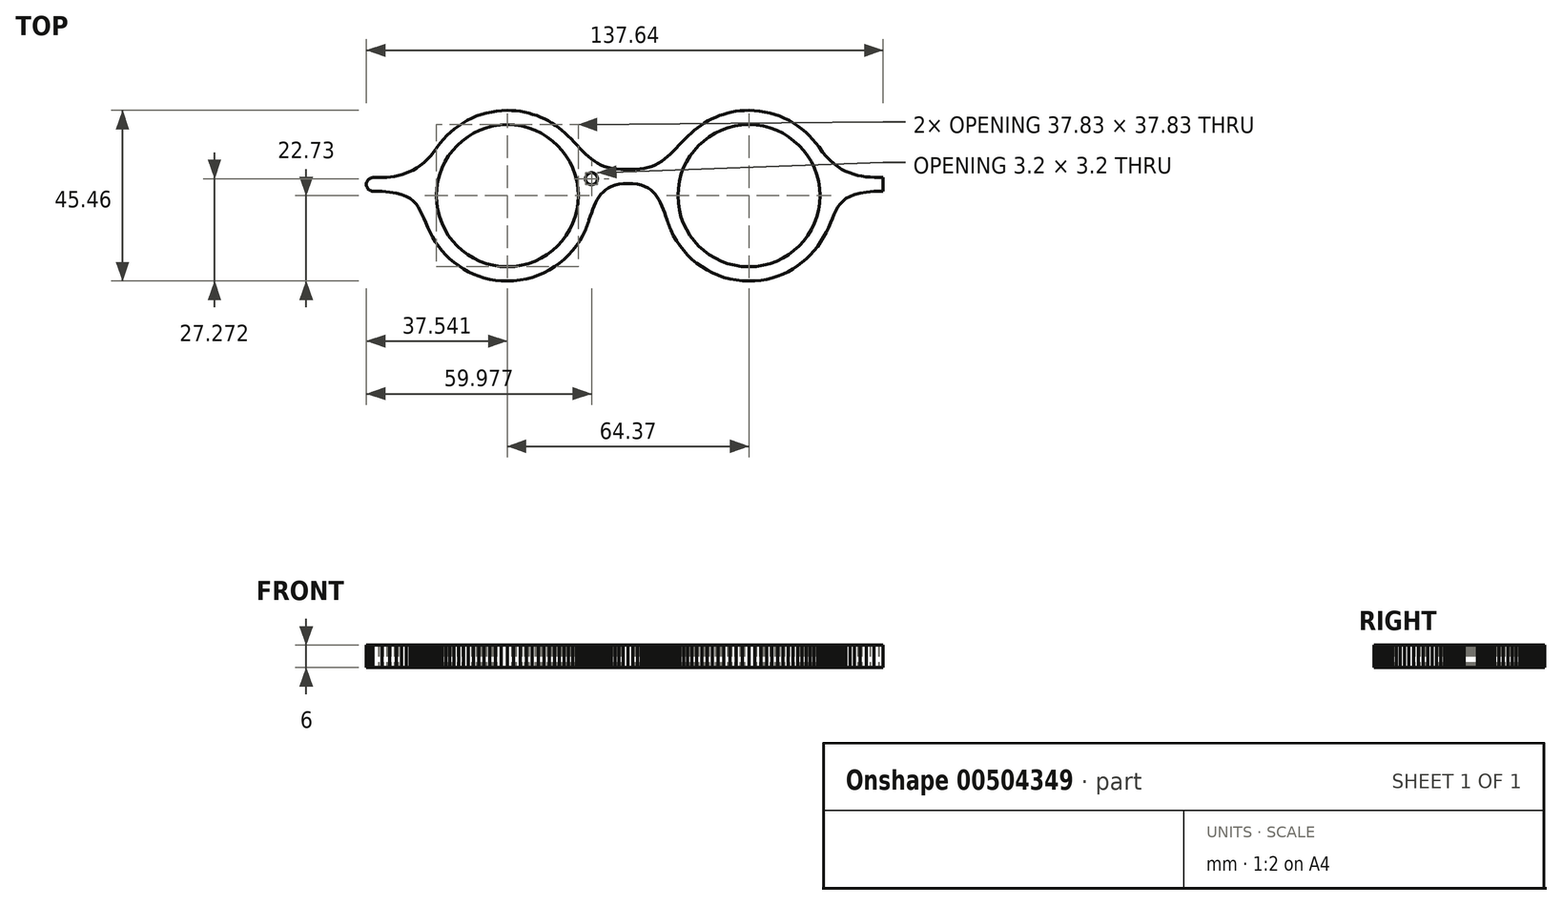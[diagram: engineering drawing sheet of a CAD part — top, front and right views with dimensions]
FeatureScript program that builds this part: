
annotation { "Feature Type Name" : "Feature", "Feature Type Description" : "" }
export const myFeature = defineFeature(function(context is Context, id is Id, definition is map)
    precondition{}
    {
        {
            var Q0;
            Q0=qCreatedBy(makeId("Top.planeOp"),FACE);
            var sketch = newSketch(context, id + "F0", { "sketchPlane" : qUnion([Q0])});
            skLineSegment(sketch, "E0", {"start": v(67.67, 4.85) * mm, "end": v(66.53, 4.88) * mm});
            skLineSegment(sketch, "E1", {"start": v(66.53, 4.88) * mm, "end": v(65.4, 4.94) * mm});
            skLineSegment(sketch, "E2", {"start": v(65.4, 4.94) * mm, "end": v(64.27, 5.05) * mm});
            skLineSegment(sketch, "E3", {"start": v(64.27, 5.05) * mm, "end": v(63.16, 5.2) * mm});
            skLineSegment(sketch, "E4", {"start": v(63.16, 5.2) * mm, "end": v(62.05, 5.43) * mm});
            skLineSegment(sketch, "E5", {"start": v(62.05, 5.43) * mm, "end": v(60.96, 5.72) * mm});
            skLineSegment(sketch, "E6", {"start": v(60.96, 5.72) * mm, "end": v(59.88, 6.09) * mm});
            skLineSegment(sketch, "E7", {"start": v(59.88, 6.09) * mm, "end": v(58.8, 6.54) * mm});
            skLineSegment(sketch, "E8", {"start": v(58.8, 6.54) * mm, "end": v(57.75, 7.1) * mm});
            skLineSegment(sketch, "E9", {"start": v(57.75, 7.1) * mm, "end": v(56.71, 7.75) * mm});
            skLineSegment(sketch, "E10", {"start": v(56.71, 7.75) * mm, "end": v(55.69, 8.53) * mm});
            skLineSegment(sketch, "E11", {"start": v(55.69, 8.53) * mm, "end": v(54.68, 9.43) * mm});
            skLineSegment(sketch, "E12", {"start": v(54.68, 9.43) * mm, "end": v(53.68, 10.46) * mm});
            skLineSegment(sketch, "E13", {"start": v(53.68, 10.46) * mm, "end": v(52.7, 11.64) * mm});
            skLineSegment(sketch, "E14", {"start": v(52.7, 11.64) * mm, "end": v(51.75, 12.97) * mm});
            skLineSegment(sketch, "E15", {"start": v(51.75, 12.97) * mm, "end": v(50.95, 14.05) * mm});
            skLineSegment(sketch, "E16", {"start": v(50.95, 14.05) * mm, "end": v(50.08, 15.08) * mm});
            skLineSegment(sketch, "E17", {"start": v(50.08, 15.08) * mm, "end": v(49.16, 16.06) * mm});
            skLineSegment(sketch, "E18", {"start": v(49.16, 16.06) * mm, "end": v(48.18, 16.98) * mm});
            skLineSegment(sketch, "E19", {"start": v(48.18, 16.98) * mm, "end": v(47.15, 17.85) * mm});
            skLineSegment(sketch, "E20", {"start": v(47.15, 17.85) * mm, "end": v(46.07, 18.65) * mm});
            skLineSegment(sketch, "E21", {"start": v(46.07, 18.65) * mm, "end": v(44.94, 19.39) * mm});
            skLineSegment(sketch, "E22", {"start": v(44.94, 19.39) * mm, "end": v(43.77, 20.06) * mm});
            skLineSegment(sketch, "E23", {"start": v(43.77, 20.06) * mm, "end": v(42.56, 20.67) * mm});
            skLineSegment(sketch, "E24", {"start": v(42.56, 20.67) * mm, "end": v(41.3, 21.2) * mm});
            skLineSegment(sketch, "E25", {"start": v(41.3, 21.2) * mm, "end": v(40.01, 21.66) * mm});
            skLineSegment(sketch, "E26", {"start": v(40.01, 21.66) * mm, "end": v(38.68, 22.04) * mm});
            skLineSegment(sketch, "E27", {"start": v(38.68, 22.04) * mm, "end": v(37.33, 22.34) * mm});
            skLineSegment(sketch, "E28", {"start": v(37.33, 22.34) * mm, "end": v(35.94, 22.56) * mm});
            skLineSegment(sketch, "E29", {"start": v(35.94, 22.56) * mm, "end": v(34.53, 22.69) * mm});
            skLineSegment(sketch, "E30", {"start": v(34.53, 22.69) * mm, "end": v(33.1, 22.73) * mm});
            skLineSegment(sketch, "E31", {"start": v(33.1, 22.73) * mm, "end": v(31.91, 22.7) * mm});
            skLineSegment(sketch, "E32", {"start": v(31.91, 22.7) * mm, "end": v(30.75, 22.61) * mm});
            skLineSegment(sketch, "E33", {"start": v(30.75, 22.61) * mm, "end": v(29.6, 22.47) * mm});
            skLineSegment(sketch, "E34", {"start": v(29.6, 22.47) * mm, "end": v(28.48, 22.26) * mm});
            skLineSegment(sketch, "E35", {"start": v(28.48, 22.26) * mm, "end": v(27.37, 22) * mm});
            skLineSegment(sketch, "E36", {"start": v(27.37, 22) * mm, "end": v(26.28, 21.7) * mm});
            skLineSegment(sketch, "E37", {"start": v(26.28, 21.7) * mm, "end": v(25.22, 21.33) * mm});
            skLineSegment(sketch, "E38", {"start": v(25.22, 21.33) * mm, "end": v(24.18, 20.91) * mm});
            skLineSegment(sketch, "E39", {"start": v(24.18, 20.91) * mm, "end": v(23.17, 20.45) * mm});
            skLineSegment(sketch, "E40", {"start": v(23.17, 20.45) * mm, "end": v(22.18, 19.94) * mm});
            skLineSegment(sketch, "E41", {"start": v(22.18, 19.94) * mm, "end": v(21.22, 19.38) * mm});
            skLineSegment(sketch, "E42", {"start": v(21.22, 19.38) * mm, "end": v(20.3, 18.78) * mm});
            skLineSegment(sketch, "E43", {"start": v(20.3, 18.78) * mm, "end": v(19.4, 18.14) * mm});
            skLineSegment(sketch, "E44", {"start": v(19.4, 18.14) * mm, "end": v(18.54, 17.45) * mm});
            skLineSegment(sketch, "E45", {"start": v(18.54, 17.45) * mm, "end": v(17.71, 16.72) * mm});
            skLineSegment(sketch, "E46", {"start": v(17.71, 16.72) * mm, "end": v(16.92, 15.96) * mm});
            skLineSegment(sketch, "E47", {"start": v(16.92, 15.96) * mm, "end": v(16.07, 15.11) * mm});
            skLineSegment(sketch, "E48", {"start": v(16.07, 15.11) * mm, "end": v(15.26, 14.27) * mm});
            skLineSegment(sketch, "E49", {"start": v(15.26, 14.27) * mm, "end": v(14.47, 13.45) * mm});
            skLineSegment(sketch, "E50", {"start": v(14.47, 13.45) * mm, "end": v(13.71, 12.66) * mm});
            skLineSegment(sketch, "E51", {"start": v(13.71, 12.66) * mm, "end": v(12.96, 11.89) * mm});
            skLineSegment(sketch, "E52", {"start": v(12.96, 11.89) * mm, "end": v(12.2, 11.15) * mm});
            skLineSegment(sketch, "E53", {"start": v(12.2, 11.15) * mm, "end": v(11.45, 10.46) * mm});
            skLineSegment(sketch, "E54", {"start": v(11.45, 10.46) * mm, "end": v(10.67, 9.81) * mm});
            skLineSegment(sketch, "E55", {"start": v(10.67, 9.81) * mm, "end": v(9.87, 9.22) * mm});
            skLineSegment(sketch, "E56", {"start": v(9.87, 9.22) * mm, "end": v(9.04, 8.68) * mm});
            skLineSegment(sketch, "E57", {"start": v(9.04, 8.68) * mm, "end": v(8.16, 8.22) * mm});
            skLineSegment(sketch, "E58", {"start": v(8.16, 8.22) * mm, "end": v(7.23, 7.82) * mm});
            skLineSegment(sketch, "E59", {"start": v(7.23, 7.82) * mm, "end": v(6.24, 7.5) * mm});
            skLineSegment(sketch, "E60", {"start": v(6.24, 7.5) * mm, "end": v(5.18, 7.26) * mm});
            skLineSegment(sketch, "E61", {"start": v(5.18, 7.26) * mm, "end": v(4.03, 7.12) * mm});
            skLineSegment(sketch, "E62", {"start": v(4.03, 7.12) * mm, "end": v(2.8, 7.07) * mm});
            skLineSegment(sketch, "E63", {"start": v(2.8, 7.07) * mm, "end": v(2.57, 7.07) * mm});
            skLineSegment(sketch, "E64", {"start": v(2.57, 7.07) * mm, "end": v(2.33, 7.07) * mm});
            skLineSegment(sketch, "E65", {"start": v(2.33, 7.07) * mm, "end": v(2.1, 7.07) * mm});
            skLineSegment(sketch, "E66", {"start": v(2.1, 7.07) * mm, "end": v(1.86, 7.07) * mm});
            skLineSegment(sketch, "E67", {"start": v(1.86, 7.07) * mm, "end": v(1.62, 7.07) * mm});
            skLineSegment(sketch, "E68", {"start": v(1.62, 7.07) * mm, "end": v(1.38, 7.07) * mm});
            skLineSegment(sketch, "E69", {"start": v(1.38, 7.07) * mm, "end": v(1.14, 7.07) * mm});
            skLineSegment(sketch, "E70", {"start": v(1.14, 7.07) * mm, "end": v(0.9, 7.07) * mm});
            skLineSegment(sketch, "E71", {"start": v(0.9, 7.07) * mm, "end": v(0.67, 7.07) * mm});
            skLineSegment(sketch, "E72", {"start": v(0.67, 7.07) * mm, "end": v(0.43, 7.07) * mm});
            skLineSegment(sketch, "E73", {"start": v(0.43, 7.07) * mm, "end": v(0.2, 7.07) * mm});
            skLineSegment(sketch, "E74", {"start": v(0.2, 7.07) * mm, "end": v(-0.04, 7.07) * mm});
            skLineSegment(sketch, "E75", {"start": v(-0.04, 7.07) * mm, "end": v(-0.28, 7.07) * mm});
            skLineSegment(sketch, "E76", {"start": v(-0.28, 7.07) * mm, "end": v(-0.52, 7.07) * mm});
            skLineSegment(sketch, "E77", {"start": v(-0.52, 7.07) * mm, "end": v(-0.75, 7.07) * mm});
            skLineSegment(sketch, "E78", {"start": v(-0.75, 7.07) * mm, "end": v(-1, 7.07) * mm});
            skLineSegment(sketch, "E79", {"start": v(-1, 7.07) * mm, "end": v(-2.22, 7.12) * mm});
            skLineSegment(sketch, "E80", {"start": v(-2.22, 7.12) * mm, "end": v(-3.36, 7.26) * mm});
            skLineSegment(sketch, "E81", {"start": v(-3.36, 7.26) * mm, "end": v(-4.43, 7.5) * mm});
            skLineSegment(sketch, "E82", {"start": v(-4.43, 7.5) * mm, "end": v(-5.42, 7.82) * mm});
            skLineSegment(sketch, "E83", {"start": v(-5.42, 7.82) * mm, "end": v(-6.35, 8.22) * mm});
            skLineSegment(sketch, "E84", {"start": v(-6.35, 8.22) * mm, "end": v(-7.23, 8.68) * mm});
            skLineSegment(sketch, "E85", {"start": v(-7.23, 8.68) * mm, "end": v(-8.06, 9.22) * mm});
            skLineSegment(sketch, "E86", {"start": v(-8.06, 9.22) * mm, "end": v(-8.86, 9.81) * mm});
            skLineSegment(sketch, "E87", {"start": v(-8.86, 9.81) * mm, "end": v(-9.64, 10.46) * mm});
            skLineSegment(sketch, "E88", {"start": v(-9.64, 10.46) * mm, "end": v(-10.4, 11.15) * mm});
            skLineSegment(sketch, "E89", {"start": v(-10.4, 11.15) * mm, "end": v(-11.15, 11.89) * mm});
            skLineSegment(sketch, "E90", {"start": v(-11.15, 11.89) * mm, "end": v(-11.9, 12.66) * mm});
            skLineSegment(sketch, "E91", {"start": v(-11.9, 12.66) * mm, "end": v(-12.66, 13.45) * mm});
            skLineSegment(sketch, "E92", {"start": v(-12.66, 13.45) * mm, "end": v(-13.45, 14.27) * mm});
            skLineSegment(sketch, "E93", {"start": v(-13.45, 14.27) * mm, "end": v(-14.26, 15.11) * mm});
            skLineSegment(sketch, "E94", {"start": v(-14.26, 15.11) * mm, "end": v(-15.1, 15.96) * mm});
            skLineSegment(sketch, "E95", {"start": v(-15.1, 15.96) * mm, "end": v(-15.9, 16.72) * mm});
            skLineSegment(sketch, "E96", {"start": v(-15.9, 16.72) * mm, "end": v(-16.73, 17.45) * mm});
            skLineSegment(sketch, "E97", {"start": v(-16.73, 17.45) * mm, "end": v(-17.59, 18.14) * mm});
            skLineSegment(sketch, "E98", {"start": v(-17.59, 18.14) * mm, "end": v(-18.48, 18.78) * mm});
            skLineSegment(sketch, "E99", {"start": v(-18.48, 18.78) * mm, "end": v(-19.41, 19.38) * mm});
            skLineSegment(sketch, "E100", {"start": v(-19.41, 19.38) * mm, "end": v(-20.37, 19.94) * mm});
            skLineSegment(sketch, "E101", {"start": v(-20.37, 19.94) * mm, "end": v(-21.36, 20.45) * mm});
            skLineSegment(sketch, "E102", {"start": v(-21.36, 20.45) * mm, "end": v(-22.37, 20.91) * mm});
            skLineSegment(sketch, "E103", {"start": v(-22.37, 20.91) * mm, "end": v(-23.4, 21.33) * mm});
            skLineSegment(sketch, "E104", {"start": v(-23.4, 21.33) * mm, "end": v(-24.47, 21.7) * mm});
            skLineSegment(sketch, "E105", {"start": v(-24.47, 21.7) * mm, "end": v(-25.56, 22) * mm});
            skLineSegment(sketch, "E106", {"start": v(-25.56, 22) * mm, "end": v(-26.67, 22.26) * mm});
            skLineSegment(sketch, "E107", {"start": v(-26.67, 22.26) * mm, "end": v(-27.8, 22.47) * mm});
            skLineSegment(sketch, "E108", {"start": v(-27.8, 22.47) * mm, "end": v(-28.94, 22.61) * mm});
            skLineSegment(sketch, "E109", {"start": v(-28.94, 22.61) * mm, "end": v(-30.1, 22.7) * mm});
            skLineSegment(sketch, "E110", {"start": v(-30.1, 22.7) * mm, "end": v(-31.28, 22.73) * mm});
            skLineSegment(sketch, "E111", {"start": v(-31.28, 22.73) * mm, "end": v(-32.72, 22.69) * mm});
            skLineSegment(sketch, "E112", {"start": v(-32.72, 22.69) * mm, "end": v(-34.13, 22.56) * mm});
            skLineSegment(sketch, "E113", {"start": v(-34.13, 22.56) * mm, "end": v(-35.51, 22.34) * mm});
            skLineSegment(sketch, "E114", {"start": v(-35.51, 22.34) * mm, "end": v(-36.87, 22.04) * mm});
            skLineSegment(sketch, "E115", {"start": v(-36.87, 22.04) * mm, "end": v(-38.2, 21.66) * mm});
            skLineSegment(sketch, "E116", {"start": v(-38.2, 21.66) * mm, "end": v(-39.49, 21.2) * mm});
            skLineSegment(sketch, "E117", {"start": v(-39.49, 21.2) * mm, "end": v(-40.74, 20.67) * mm});
            skLineSegment(sketch, "E118", {"start": v(-40.74, 20.67) * mm, "end": v(-41.96, 20.06) * mm});
            skLineSegment(sketch, "E119", {"start": v(-41.96, 20.06) * mm, "end": v(-43.13, 19.39) * mm});
            skLineSegment(sketch, "E120", {"start": v(-43.13, 19.39) * mm, "end": v(-44.26, 18.65) * mm});
            skLineSegment(sketch, "E121", {"start": v(-44.26, 18.65) * mm, "end": v(-45.34, 17.85) * mm});
            skLineSegment(sketch, "E122", {"start": v(-45.34, 17.85) * mm, "end": v(-46.37, 16.98) * mm});
            skLineSegment(sketch, "E123", {"start": v(-46.37, 16.98) * mm, "end": v(-47.35, 16.06) * mm});
            skLineSegment(sketch, "E124", {"start": v(-47.35, 16.06) * mm, "end": v(-48.27, 15.08) * mm});
            skLineSegment(sketch, "E125", {"start": v(-48.27, 15.08) * mm, "end": v(-49.13, 14.05) * mm});
            skLineSegment(sketch, "E126", {"start": v(-49.13, 14.05) * mm, "end": v(-49.94, 12.97) * mm});
            skLineSegment(sketch, "E127", {"start": v(-49.94, 12.97) * mm, "end": v(-50.81, 11.74) * mm});
            skLineSegment(sketch, "E128", {"start": v(-50.81, 11.74) * mm, "end": v(-51.7, 10.64) * mm});
            skLineSegment(sketch, "E129", {"start": v(-51.7, 10.64) * mm, "end": v(-52.62, 9.67) * mm});
            skLineSegment(sketch, "E130", {"start": v(-52.62, 9.67) * mm, "end": v(-53.54, 8.8) * mm});
            skLineSegment(sketch, "E131", {"start": v(-53.54, 8.8) * mm, "end": v(-54.48, 8.05) * mm});
            skLineSegment(sketch, "E132", {"start": v(-54.48, 8.05) * mm, "end": v(-55.44, 7.4) * mm});
            skLineSegment(sketch, "E133", {"start": v(-55.44, 7.4) * mm, "end": v(-56.4, 6.83) * mm});
            skLineSegment(sketch, "E134", {"start": v(-56.4, 6.83) * mm, "end": v(-57.37, 6.35) * mm});
            skLineSegment(sketch, "E135", {"start": v(-57.37, 6.35) * mm, "end": v(-58.36, 5.96) * mm});
            skLineSegment(sketch, "E136", {"start": v(-58.36, 5.96) * mm, "end": v(-59.36, 5.63) * mm});
            skLineSegment(sketch, "E137", {"start": v(-59.36, 5.63) * mm, "end": v(-60.36, 5.38) * mm});
            skLineSegment(sketch, "E138", {"start": v(-60.36, 5.38) * mm, "end": v(-61.38, 5.18) * mm});
            skLineSegment(sketch, "E139", {"start": v(-61.38, 5.18) * mm, "end": v(-62.4, 5.03) * mm});
            skLineSegment(sketch, "E140", {"start": v(-62.4, 5.03) * mm, "end": v(-63.43, 4.93) * mm});
            skLineSegment(sketch, "E141", {"start": v(-63.43, 4.93) * mm, "end": v(-64.46, 4.87) * mm});
            skLineSegment(sketch, "E142", {"start": v(-64.46, 4.87) * mm, "end": v(-65.5, 4.85) * mm});
            skLineSegment(sketch, "E143", {"start": v(-65.5, 4.85) * mm, "end": v(-65.6, 4.84) * mm});
            skLineSegment(sketch, "E144", {"start": v(-65.6, 4.84) * mm, "end": v(-65.69, 4.84) * mm});
            skLineSegment(sketch, "E145", {"start": v(-65.69, 4.84) * mm, "end": v(-65.78, 4.84) * mm});
            skLineSegment(sketch, "E146", {"start": v(-65.78, 4.84) * mm, "end": v(-65.88, 4.84) * mm});
            skLineSegment(sketch, "E147", {"start": v(-65.88, 4.84) * mm, "end": v(-65.97, 4.84) * mm});
            skLineSegment(sketch, "E148", {"start": v(-65.97, 4.84) * mm, "end": v(-66.07, 4.84) * mm});
            skLineSegment(sketch, "E149", {"start": v(-66.07, 4.84) * mm, "end": v(-66.16, 4.84) * mm});
            skLineSegment(sketch, "E150", {"start": v(-66.16, 4.84) * mm, "end": v(-66.26, 4.84) * mm});
            skLineSegment(sketch, "E151", {"start": v(-66.26, 4.84) * mm, "end": v(-66.35, 4.84) * mm});
            skLineSegment(sketch, "E152", {"start": v(-66.35, 4.84) * mm, "end": v(-66.44, 4.84) * mm});
            skLineSegment(sketch, "E153", {"start": v(-66.44, 4.84) * mm, "end": v(-66.54, 4.84) * mm});
            skLineSegment(sketch, "E154", {"start": v(-66.54, 4.84) * mm, "end": v(-66.63, 4.84) * mm});
            skLineSegment(sketch, "E155", {"start": v(-66.63, 4.84) * mm, "end": v(-66.73, 4.84) * mm});
            skLineSegment(sketch, "E156", {"start": v(-66.73, 4.84) * mm, "end": v(-66.82, 4.84) * mm});
            skLineSegment(sketch, "E157", {"start": v(-66.82, 4.84) * mm, "end": v(-66.92, 4.84) * mm});
            skLineSegment(sketch, "E158", {"start": v(-66.92, 4.84) * mm, "end": v(-67.01, 4.84) * mm});
            skLineSegment(sketch, "E159", {"start": v(-67.01, 4.84) * mm, "end": v(-67.01, 4.84) * mm});
            skLineSegment(sketch, "E160", {"start": v(-67.01, 4.84) * mm, "end": v(-67.2, 4.83) * mm});
            skLineSegment(sketch, "E161", {"start": v(-67.2, 4.83) * mm, "end": v(-67.38, 4.8) * mm});
            skLineSegment(sketch, "E162", {"start": v(-67.38, 4.8) * mm, "end": v(-67.55, 4.75) * mm});
            skLineSegment(sketch, "E163", {"start": v(-67.55, 4.75) * mm, "end": v(-67.72, 4.7) * mm});
            skLineSegment(sketch, "E164", {"start": v(-67.72, 4.7) * mm, "end": v(-67.87, 4.62) * mm});
            skLineSegment(sketch, "E165", {"start": v(-67.87, 4.62) * mm, "end": v(-68.02, 4.53) * mm});
            skLineSegment(sketch, "E166", {"start": v(-68.02, 4.53) * mm, "end": v(-68.16, 4.42) * mm});
            skLineSegment(sketch, "E167", {"start": v(-68.16, 4.42) * mm, "end": v(-68.3, 4.3) * mm});
            skLineSegment(sketch, "E168", {"start": v(-68.3, 4.3) * mm, "end": v(-68.4, 4.18) * mm});
            skLineSegment(sketch, "E169", {"start": v(-68.4, 4.18) * mm, "end": v(-68.51, 4.04) * mm});
            skLineSegment(sketch, "E170", {"start": v(-68.51, 4.04) * mm, "end": v(-68.6, 3.89) * mm});
            skLineSegment(sketch, "E171", {"start": v(-68.6, 3.89) * mm, "end": v(-68.68, 3.73) * mm});
            skLineSegment(sketch, "E172", {"start": v(-68.68, 3.73) * mm, "end": v(-68.74, 3.56) * mm});
            skLineSegment(sketch, "E173", {"start": v(-68.74, 3.56) * mm, "end": v(-68.79, 3.39) * mm});
            skLineSegment(sketch, "E174", {"start": v(-68.79, 3.39) * mm, "end": v(-68.81, 3.2) * mm});
            skLineSegment(sketch, "E175", {"start": v(-68.81, 3.2) * mm, "end": v(-68.82, 3.02) * mm});
            skLineSegment(sketch, "E176", {"start": v(-68.82, 3.02) * mm, "end": v(-68.81, 2.84) * mm});
            skLineSegment(sketch, "E177", {"start": v(-68.81, 2.84) * mm, "end": v(-68.79, 2.66) * mm});
            skLineSegment(sketch, "E178", {"start": v(-68.79, 2.66) * mm, "end": v(-68.74, 2.48) * mm});
            skLineSegment(sketch, "E179", {"start": v(-68.74, 2.48) * mm, "end": v(-68.68, 2.32) * mm});
            skLineSegment(sketch, "E180", {"start": v(-68.68, 2.32) * mm, "end": v(-68.6, 2.16) * mm});
            skLineSegment(sketch, "E181", {"start": v(-68.6, 2.16) * mm, "end": v(-68.51, 2) * mm});
            skLineSegment(sketch, "E182", {"start": v(-68.51, 2) * mm, "end": v(-68.4, 1.87) * mm});
            skLineSegment(sketch, "E183", {"start": v(-68.4, 1.87) * mm, "end": v(-68.3, 1.74) * mm});
            skLineSegment(sketch, "E184", {"start": v(-68.3, 1.74) * mm, "end": v(-68.16, 1.62) * mm});
            skLineSegment(sketch, "E185", {"start": v(-68.16, 1.62) * mm, "end": v(-68.02, 1.52) * mm});
            skLineSegment(sketch, "E186", {"start": v(-68.02, 1.52) * mm, "end": v(-67.87, 1.43) * mm});
            skLineSegment(sketch, "E187", {"start": v(-67.87, 1.43) * mm, "end": v(-67.72, 1.35) * mm});
            skLineSegment(sketch, "E188", {"start": v(-67.72, 1.35) * mm, "end": v(-67.55, 1.3) * mm});
            skLineSegment(sketch, "E189", {"start": v(-67.55, 1.3) * mm, "end": v(-67.38, 1.25) * mm});
            skLineSegment(sketch, "E190", {"start": v(-67.38, 1.25) * mm, "end": v(-67.2, 1.22) * mm});
            skLineSegment(sketch, "E191", {"start": v(-67.2, 1.22) * mm, "end": v(-67.01, 1.21) * mm});
            skLineSegment(sketch, "E192", {"start": v(-67.01, 1.21) * mm, "end": v(-67.01, 1.21) * mm});
            skLineSegment(sketch, "E193", {"start": v(-67.01, 1.21) * mm, "end": v(-67.01, 1.2) * mm});
            skLineSegment(sketch, "E194", {"start": v(-67.01, 1.2) * mm, "end": v(-64.65, 1.15) * mm});
            skLineSegment(sketch, "E195", {"start": v(-64.65, 1.15) * mm, "end": v(-62.62, 0.98) * mm});
            skLineSegment(sketch, "E196", {"start": v(-62.62, 0.98) * mm, "end": v(-60.88, 0.7) * mm});
            skLineSegment(sketch, "E197", {"start": v(-60.88, 0.7) * mm, "end": v(-59.41, 0.31) * mm});
            skLineSegment(sketch, "E198", {"start": v(-59.41, 0.31) * mm, "end": v(-58.18, -0.18) * mm});
            skLineSegment(sketch, "E199", {"start": v(-58.18, -0.18) * mm, "end": v(-57.15, -0.76) * mm});
            skLineSegment(sketch, "E200", {"start": v(-57.15, -0.76) * mm, "end": v(-56.3, -1.44) * mm});
            skLineSegment(sketch, "E201", {"start": v(-56.3, -1.44) * mm, "end": v(-55.57, -2.2) * mm});
            skLineSegment(sketch, "E202", {"start": v(-55.57, -2.2) * mm, "end": v(-54.97, -3.05) * mm});
            skLineSegment(sketch, "E203", {"start": v(-54.97, -3.05) * mm, "end": v(-54.44, -3.98) * mm});
            skLineSegment(sketch, "E204", {"start": v(-54.44, -3.98) * mm, "end": v(-53.96, -4.98) * mm});
            skLineSegment(sketch, "E205", {"start": v(-53.96, -4.98) * mm, "end": v(-53.5, -6.06) * mm});
            skLineSegment(sketch, "E206", {"start": v(-53.5, -6.06) * mm, "end": v(-53.01, -7.2) * mm});
            skLineSegment(sketch, "E207", {"start": v(-53.01, -7.2) * mm, "end": v(-52.49, -8.4) * mm});
            skLineSegment(sketch, "E208", {"start": v(-52.49, -8.4) * mm, "end": v(-51.89, -9.67) * mm});
            skLineSegment(sketch, "E209", {"start": v(-51.89, -9.67) * mm, "end": v(-51.17, -10.99) * mm});
            skLineSegment(sketch, "E210", {"start": v(-51.17, -10.99) * mm, "end": v(-50.4, -12.27) * mm});
            skLineSegment(sketch, "E211", {"start": v(-50.4, -12.27) * mm, "end": v(-49.56, -13.5) * mm});
            skLineSegment(sketch, "E212", {"start": v(-49.56, -13.5) * mm, "end": v(-48.63, -14.67) * mm});
            skLineSegment(sketch, "E213", {"start": v(-48.63, -14.67) * mm, "end": v(-47.63, -15.77) * mm});
            skLineSegment(sketch, "E214", {"start": v(-47.63, -15.77) * mm, "end": v(-46.56, -16.81) * mm});
            skLineSegment(sketch, "E215", {"start": v(-46.56, -16.81) * mm, "end": v(-45.43, -17.78) * mm});
            skLineSegment(sketch, "E216", {"start": v(-45.43, -17.78) * mm, "end": v(-44.23, -18.67) * mm});
            skLineSegment(sketch, "E217", {"start": v(-44.23, -18.67) * mm, "end": v(-42.98, -19.48) * mm});
            skLineSegment(sketch, "E218", {"start": v(-42.98, -19.48) * mm, "end": v(-41.67, -20.22) * mm});
            skLineSegment(sketch, "E219", {"start": v(-41.67, -20.22) * mm, "end": v(-40.3, -20.86) * mm});
            skLineSegment(sketch, "E220", {"start": v(-40.3, -20.86) * mm, "end": v(-38.9, -21.42) * mm});
            skLineSegment(sketch, "E221", {"start": v(-38.9, -21.42) * mm, "end": v(-37.45, -21.88) * mm});
            skLineSegment(sketch, "E222", {"start": v(-37.45, -21.88) * mm, "end": v(-35.96, -22.25) * mm});
            skLineSegment(sketch, "E223", {"start": v(-35.96, -22.25) * mm, "end": v(-34.43, -22.52) * mm});
            skLineSegment(sketch, "E224", {"start": v(-34.43, -22.52) * mm, "end": v(-32.87, -22.68) * mm});
            skLineSegment(sketch, "E225", {"start": v(-32.87, -22.68) * mm, "end": v(-31.28, -22.73) * mm});
            skLineSegment(sketch, "E226", {"start": v(-31.28, -22.73) * mm, "end": v(-29.55, -22.67) * mm});
            skLineSegment(sketch, "E227", {"start": v(-29.55, -22.67) * mm, "end": v(-27.86, -22.48) * mm});
            skLineSegment(sketch, "E228", {"start": v(-27.86, -22.48) * mm, "end": v(-26.2, -22.16) * mm});
            skLineSegment(sketch, "E229", {"start": v(-26.2, -22.16) * mm, "end": v(-24.6, -21.73) * mm});
            skLineSegment(sketch, "E230", {"start": v(-24.6, -21.73) * mm, "end": v(-23.04, -21.19) * mm});
            skLineSegment(sketch, "E231", {"start": v(-23.04, -21.19) * mm, "end": v(-21.53, -20.53) * mm});
            skLineSegment(sketch, "E232", {"start": v(-21.53, -20.53) * mm, "end": v(-20.08, -19.78) * mm});
            skLineSegment(sketch, "E233", {"start": v(-20.08, -19.78) * mm, "end": v(-18.7, -18.92) * mm});
            skLineSegment(sketch, "E234", {"start": v(-18.7, -18.92) * mm, "end": v(-17.38, -17.97) * mm});
            skLineSegment(sketch, "E235", {"start": v(-17.38, -17.97) * mm, "end": v(-16.13, -16.94) * mm});
            skLineSegment(sketch, "E236", {"start": v(-16.13, -16.94) * mm, "end": v(-14.97, -15.81) * mm});
            skLineSegment(sketch, "E237", {"start": v(-14.97, -15.81) * mm, "end": v(-13.88, -14.61) * mm});
            skLineSegment(sketch, "E238", {"start": v(-13.88, -14.61) * mm, "end": v(-12.88, -13.33) * mm});
            skLineSegment(sketch, "E239", {"start": v(-12.88, -13.33) * mm, "end": v(-11.97, -11.99) * mm});
            skLineSegment(sketch, "E240", {"start": v(-11.97, -11.99) * mm, "end": v(-11.16, -10.57) * mm});
            skLineSegment(sketch, "E241", {"start": v(-11.16, -10.57) * mm, "end": v(-10.45, -9.1) * mm});
            skLineSegment(sketch, "E242", {"start": v(-10.45, -9.1) * mm, "end": v(-10.38, -8.94) * mm});
            skLineSegment(sketch, "E243", {"start": v(-10.38, -8.94) * mm, "end": v(-10.31, -8.78) * mm});
            skLineSegment(sketch, "E244", {"start": v(-10.31, -8.78) * mm, "end": v(-10.25, -8.62) * mm});
            skLineSegment(sketch, "E245", {"start": v(-10.25, -8.62) * mm, "end": v(-10.18, -8.45) * mm});
            skLineSegment(sketch, "E246", {"start": v(-10.18, -8.45) * mm, "end": v(-10.12, -8.29) * mm});
            skLineSegment(sketch, "E247", {"start": v(-10.12, -8.29) * mm, "end": v(-10.05, -8.12) * mm});
            skLineSegment(sketch, "E248", {"start": v(-10.05, -8.12) * mm, "end": v(-9.99, -7.95) * mm});
            skLineSegment(sketch, "E249", {"start": v(-9.99, -7.95) * mm, "end": v(-9.93, -7.79) * mm});
            skLineSegment(sketch, "E250", {"start": v(-9.93, -7.79) * mm, "end": v(-9.87, -7.62) * mm});
            skLineSegment(sketch, "E251", {"start": v(-9.87, -7.62) * mm, "end": v(-9.8, -7.45) * mm});
            skLineSegment(sketch, "E252", {"start": v(-9.8, -7.45) * mm, "end": v(-9.75, -7.28) * mm});
            skLineSegment(sketch, "E253", {"start": v(-9.75, -7.28) * mm, "end": v(-9.7, -7.11) * mm});
            skLineSegment(sketch, "E254", {"start": v(-9.7, -7.11) * mm, "end": v(-9.64, -6.94) * mm});
            skLineSegment(sketch, "E255", {"start": v(-9.64, -6.94) * mm, "end": v(-9.58, -6.78) * mm});
            skLineSegment(sketch, "E256", {"start": v(-9.58, -6.78) * mm, "end": v(-9.53, -6.6) * mm});
            skLineSegment(sketch, "E257", {"start": v(-9.53, -6.6) * mm, "end": v(-9.48, -6.44) * mm});
            skLineSegment(sketch, "E258", {"start": v(-9.48, -6.44) * mm, "end": v(-9.15, -5.47) * mm});
            skLineSegment(sketch, "E259", {"start": v(-9.15, -5.47) * mm, "end": v(-8.82, -4.52) * mm});
            skLineSegment(sketch, "E260", {"start": v(-8.82, -4.52) * mm, "end": v(-8.48, -3.6) * mm});
            skLineSegment(sketch, "E261", {"start": v(-8.48, -3.6) * mm, "end": v(-8.13, -2.72) * mm});
            skLineSegment(sketch, "E262", {"start": v(-8.13, -2.72) * mm, "end": v(-7.75, -1.87) * mm});
            skLineSegment(sketch, "E263", {"start": v(-7.75, -1.87) * mm, "end": v(-7.33, -1.07) * mm});
            skLineSegment(sketch, "E264", {"start": v(-7.33, -1.07) * mm, "end": v(-6.87, -0.32) * mm});
            skLineSegment(sketch, "E265", {"start": v(-6.87, -0.32) * mm, "end": v(-6.35, 0.37) * mm});
            skLineSegment(sketch, "E266", {"start": v(-6.35, 0.37) * mm, "end": v(-5.77, 1) * mm});
            skLineSegment(sketch, "E267", {"start": v(-5.77, 1) * mm, "end": v(-5.11, 1.57) * mm});
            skLineSegment(sketch, "E268", {"start": v(-5.11, 1.57) * mm, "end": v(-4.38, 2.06) * mm});
            skLineSegment(sketch, "E269", {"start": v(-4.38, 2.06) * mm, "end": v(-3.54, 2.47) * mm});
            skLineSegment(sketch, "E270", {"start": v(-3.54, 2.47) * mm, "end": v(-2.6, 2.8) * mm});
            skLineSegment(sketch, "E271", {"start": v(-2.6, 2.8) * mm, "end": v(-1.56, 3.05) * mm});
            skLineSegment(sketch, "E272", {"start": v(-1.56, 3.05) * mm, "end": v(-0.4, 3.2) * mm});
            skLineSegment(sketch, "E273", {"start": v(-0.4, 3.2) * mm, "end": v(0.9, 3.25) * mm});
            skLineSegment(sketch, "E274", {"start": v(0.9, 3.25) * mm, "end": v(2.2, 3.2) * mm});
            skLineSegment(sketch, "E275", {"start": v(2.2, 3.2) * mm, "end": v(3.37, 3.05) * mm});
            skLineSegment(sketch, "E276", {"start": v(3.37, 3.05) * mm, "end": v(4.42, 2.8) * mm});
            skLineSegment(sketch, "E277", {"start": v(4.42, 2.8) * mm, "end": v(5.36, 2.47) * mm});
            skLineSegment(sketch, "E278", {"start": v(5.36, 2.47) * mm, "end": v(6.19, 2.06) * mm});
            skLineSegment(sketch, "E279", {"start": v(6.19, 2.06) * mm, "end": v(6.93, 1.57) * mm});
            skLineSegment(sketch, "E280", {"start": v(6.93, 1.57) * mm, "end": v(7.58, 1) * mm});
            skLineSegment(sketch, "E281", {"start": v(7.58, 1) * mm, "end": v(8.16, 0.37) * mm});
            skLineSegment(sketch, "E282", {"start": v(8.16, 0.37) * mm, "end": v(8.68, -0.32) * mm});
            skLineSegment(sketch, "E283", {"start": v(8.68, -0.32) * mm, "end": v(9.14, -1.07) * mm});
            skLineSegment(sketch, "E284", {"start": v(9.14, -1.07) * mm, "end": v(9.56, -1.87) * mm});
            skLineSegment(sketch, "E285", {"start": v(9.56, -1.87) * mm, "end": v(9.94, -2.72) * mm});
            skLineSegment(sketch, "E286", {"start": v(9.94, -2.72) * mm, "end": v(10.3, -3.6) * mm});
            skLineSegment(sketch, "E287", {"start": v(10.3, -3.6) * mm, "end": v(10.63, -4.52) * mm});
            skLineSegment(sketch, "E288", {"start": v(10.63, -4.52) * mm, "end": v(10.96, -5.47) * mm});
            skLineSegment(sketch, "E289", {"start": v(10.96, -5.47) * mm, "end": v(11.3, -6.44) * mm});
            skLineSegment(sketch, "E290", {"start": v(11.3, -6.44) * mm, "end": v(11.34, -6.6) * mm});
            skLineSegment(sketch, "E291", {"start": v(11.34, -6.6) * mm, "end": v(11.4, -6.78) * mm});
            skLineSegment(sketch, "E292", {"start": v(11.4, -6.78) * mm, "end": v(11.45, -6.94) * mm});
            skLineSegment(sketch, "E293", {"start": v(11.45, -6.94) * mm, "end": v(11.5, -7.11) * mm});
            skLineSegment(sketch, "E294", {"start": v(11.5, -7.11) * mm, "end": v(11.56, -7.28) * mm});
            skLineSegment(sketch, "E295", {"start": v(11.56, -7.28) * mm, "end": v(11.62, -7.45) * mm});
            skLineSegment(sketch, "E296", {"start": v(11.62, -7.45) * mm, "end": v(11.68, -7.62) * mm});
            skLineSegment(sketch, "E297", {"start": v(11.68, -7.62) * mm, "end": v(11.74, -7.79) * mm});
            skLineSegment(sketch, "E298", {"start": v(11.74, -7.79) * mm, "end": v(11.8, -7.95) * mm});
            skLineSegment(sketch, "E299", {"start": v(11.8, -7.95) * mm, "end": v(11.86, -8.12) * mm});
            skLineSegment(sketch, "E300", {"start": v(11.86, -8.12) * mm, "end": v(11.93, -8.29) * mm});
            skLineSegment(sketch, "E301", {"start": v(11.93, -8.29) * mm, "end": v(12, -8.45) * mm});
            skLineSegment(sketch, "E302", {"start": v(12, -8.45) * mm, "end": v(12.06, -8.62) * mm});
            skLineSegment(sketch, "E303", {"start": v(12.06, -8.62) * mm, "end": v(12.13, -8.78) * mm});
            skLineSegment(sketch, "E304", {"start": v(12.13, -8.78) * mm, "end": v(12.2, -8.94) * mm});
            skLineSegment(sketch, "E305", {"start": v(12.2, -8.94) * mm, "end": v(12.26, -9.1) * mm});
            skLineSegment(sketch, "E306", {"start": v(12.26, -9.1) * mm, "end": v(12.97, -10.57) * mm});
            skLineSegment(sketch, "E307", {"start": v(12.97, -10.57) * mm, "end": v(13.79, -11.99) * mm});
            skLineSegment(sketch, "E308", {"start": v(13.79, -11.99) * mm, "end": v(14.7, -13.33) * mm});
            skLineSegment(sketch, "E309", {"start": v(14.7, -13.33) * mm, "end": v(15.7, -14.61) * mm});
            skLineSegment(sketch, "E310", {"start": v(15.7, -14.61) * mm, "end": v(16.78, -15.81) * mm});
            skLineSegment(sketch, "E311", {"start": v(16.78, -15.81) * mm, "end": v(17.95, -16.94) * mm});
            skLineSegment(sketch, "E312", {"start": v(17.95, -16.94) * mm, "end": v(19.2, -17.97) * mm});
            skLineSegment(sketch, "E313", {"start": v(19.2, -17.97) * mm, "end": v(20.5, -18.92) * mm});
            skLineSegment(sketch, "E314", {"start": v(20.5, -18.92) * mm, "end": v(21.9, -19.78) * mm});
            skLineSegment(sketch, "E315", {"start": v(21.9, -19.78) * mm, "end": v(23.34, -20.53) * mm});
            skLineSegment(sketch, "E316", {"start": v(23.34, -20.53) * mm, "end": v(24.85, -21.19) * mm});
            skLineSegment(sketch, "E317", {"start": v(24.85, -21.19) * mm, "end": v(26.4, -21.73) * mm});
            skLineSegment(sketch, "E318", {"start": v(26.4, -21.73) * mm, "end": v(28.02, -22.16) * mm});
            skLineSegment(sketch, "E319", {"start": v(28.02, -22.16) * mm, "end": v(29.67, -22.48) * mm});
            skLineSegment(sketch, "E320", {"start": v(29.67, -22.48) * mm, "end": v(31.36, -22.67) * mm});
            skLineSegment(sketch, "E321", {"start": v(31.36, -22.67) * mm, "end": v(33.1, -22.73) * mm});
            skLineSegment(sketch, "E322", {"start": v(33.1, -22.73) * mm, "end": v(34.68, -22.68) * mm});
            skLineSegment(sketch, "E323", {"start": v(34.68, -22.68) * mm, "end": v(36.24, -22.52) * mm});
            skLineSegment(sketch, "E324", {"start": v(36.24, -22.52) * mm, "end": v(37.77, -22.25) * mm});
            skLineSegment(sketch, "E325", {"start": v(37.77, -22.25) * mm, "end": v(39.26, -21.88) * mm});
            skLineSegment(sketch, "E326", {"start": v(39.26, -21.88) * mm, "end": v(40.71, -21.42) * mm});
            skLineSegment(sketch, "E327", {"start": v(40.71, -21.42) * mm, "end": v(42.12, -20.86) * mm});
            skLineSegment(sketch, "E328", {"start": v(42.12, -20.86) * mm, "end": v(43.48, -20.22) * mm});
            skLineSegment(sketch, "E329", {"start": v(43.48, -20.22) * mm, "end": v(44.8, -19.49) * mm});
            skLineSegment(sketch, "E330", {"start": v(44.8, -19.49) * mm, "end": v(46.04, -18.68) * mm});
            skLineSegment(sketch, "E331", {"start": v(46.04, -18.68) * mm, "end": v(47.24, -17.78) * mm});
            skLineSegment(sketch, "E332", {"start": v(47.24, -17.78) * mm, "end": v(48.37, -16.82) * mm});
            skLineSegment(sketch, "E333", {"start": v(48.37, -16.82) * mm, "end": v(49.44, -15.78) * mm});
            skLineSegment(sketch, "E334", {"start": v(49.44, -15.78) * mm, "end": v(50.44, -14.68) * mm});
            skLineSegment(sketch, "E335", {"start": v(50.44, -14.68) * mm, "end": v(51.37, -13.5) * mm});
            skLineSegment(sketch, "E336", {"start": v(51.37, -13.5) * mm, "end": v(52.22, -12.28) * mm});
            skLineSegment(sketch, "E337", {"start": v(52.22, -12.28) * mm, "end": v(52.99, -11) * mm});
            skLineSegment(sketch, "E338", {"start": v(52.99, -11) * mm, "end": v(53.7, -9.68) * mm});
            skLineSegment(sketch, "E339", {"start": v(53.7, -9.68) * mm, "end": v(54.3, -8.41) * mm});
            skLineSegment(sketch, "E340", {"start": v(54.3, -8.41) * mm, "end": v(54.83, -7.2) * mm});
            skLineSegment(sketch, "E341", {"start": v(54.83, -7.2) * mm, "end": v(55.3, -6.07) * mm});
            skLineSegment(sketch, "E342", {"start": v(55.3, -6.07) * mm, "end": v(55.77, -4.99) * mm});
            skLineSegment(sketch, "E343", {"start": v(55.77, -4.99) * mm, "end": v(56.25, -3.99) * mm});
            skLineSegment(sketch, "E344", {"start": v(56.25, -3.99) * mm, "end": v(56.78, -3.06) * mm});
            skLineSegment(sketch, "E345", {"start": v(56.78, -3.06) * mm, "end": v(57.39, -2.2) * mm});
            skLineSegment(sketch, "E346", {"start": v(57.39, -2.2) * mm, "end": v(58.1, -1.44) * mm});
            skLineSegment(sketch, "E347", {"start": v(58.1, -1.44) * mm, "end": v(58.96, -0.76) * mm});
            skLineSegment(sketch, "E348", {"start": v(58.96, -0.76) * mm, "end": v(60, -0.18) * mm});
            skLineSegment(sketch, "E349", {"start": v(60, -0.18) * mm, "end": v(61.23, 0.31) * mm});
            skLineSegment(sketch, "E350", {"start": v(61.23, 0.31) * mm, "end": v(62.7, 0.7) * mm});
            skLineSegment(sketch, "E351", {"start": v(62.7, 0.7) * mm, "end": v(64.43, 0.98) * mm});
            skLineSegment(sketch, "E352", {"start": v(64.43, 0.98) * mm, "end": v(66.46, 1.15) * mm});
            skLineSegment(sketch, "E353", {"start": v(66.46, 1.15) * mm, "end": v(68.82, 1.2) * mm});
            skLineSegment(sketch, "E354", {"start": v(68.82, 1.2) * mm, "end": v(68.82, 1.61) * mm});
            skLineSegment(sketch, "E355", {"start": v(68.82, 1.61) * mm, "end": v(68.82, 1.95) * mm});
            skLineSegment(sketch, "E356", {"start": v(68.82, 1.95) * mm, "end": v(68.82, 2.22) * mm});
            skLineSegment(sketch, "E357", {"start": v(68.82, 2.22) * mm, "end": v(68.82, 2.45) * mm});
            skLineSegment(sketch, "E358", {"start": v(68.82, 2.45) * mm, "end": v(68.82, 2.64) * mm});
            skLineSegment(sketch, "E359", {"start": v(68.82, 2.64) * mm, "end": v(68.82, 2.8) * mm});
            skLineSegment(sketch, "E360", {"start": v(68.82, 2.8) * mm, "end": v(68.82, 2.93) * mm});
            skLineSegment(sketch, "E361", {"start": v(68.82, 2.93) * mm, "end": v(68.82, 3.05) * mm});
            skLineSegment(sketch, "E362", {"start": v(68.82, 3.05) * mm, "end": v(68.82, 3.18) * mm});
            skLineSegment(sketch, "E363", {"start": v(68.82, 3.18) * mm, "end": v(68.82, 3.31) * mm});
            skLineSegment(sketch, "E364", {"start": v(68.82, 3.31) * mm, "end": v(68.82, 3.46) * mm});
            skLineSegment(sketch, "E365", {"start": v(68.82, 3.46) * mm, "end": v(68.82, 3.64) * mm});
            skLineSegment(sketch, "E366", {"start": v(68.82, 3.64) * mm, "end": v(68.82, 3.86) * mm});
            skLineSegment(sketch, "E367", {"start": v(68.82, 3.86) * mm, "end": v(68.82, 4.13) * mm});
            skLineSegment(sketch, "E368", {"start": v(68.82, 4.13) * mm, "end": v(68.82, 4.45) * mm});
            skLineSegment(sketch, "E369", {"start": v(68.82, 4.45) * mm, "end": v(68.82, 4.84) * mm});
            skLineSegment(sketch, "E370", {"start": v(68.82, 4.84) * mm, "end": v(67.67, 4.85) * mm});
            skLineSegment(sketch, "E371", {"start": v(-12.46, -1.93) * mm, "end": v(-12.75, -3.8) * mm});
            skLineSegment(sketch, "E372", {"start": v(-12.75, -3.8) * mm, "end": v(-13.21, -5.62) * mm});
            skLineSegment(sketch, "E373", {"start": v(-13.21, -5.62) * mm, "end": v(-13.85, -7.36) * mm});
            skLineSegment(sketch, "E374", {"start": v(-13.85, -7.36) * mm, "end": v(-14.65, -9) * mm});
            skLineSegment(sketch, "E375", {"start": v(-14.65, -9) * mm, "end": v(-15.6, -10.57) * mm});
            skLineSegment(sketch, "E376", {"start": v(-15.6, -10.57) * mm, "end": v(-16.69, -12.03) * mm});
            skLineSegment(sketch, "E377", {"start": v(-16.69, -12.03) * mm, "end": v(-17.9, -13.37) * mm});
            skLineSegment(sketch, "E378", {"start": v(-17.9, -13.37) * mm, "end": v(-19.25, -14.6) * mm});
            skLineSegment(sketch, "E379", {"start": v(-19.25, -14.6) * mm, "end": v(-20.7, -15.68) * mm});
            skLineSegment(sketch, "E380", {"start": v(-20.7, -15.68) * mm, "end": v(-22.27, -16.63) * mm});
            skLineSegment(sketch, "E381", {"start": v(-22.27, -16.63) * mm, "end": v(-23.92, -17.43) * mm});
            skLineSegment(sketch, "E382", {"start": v(-23.92, -17.43) * mm, "end": v(-25.66, -18.07) * mm});
            skLineSegment(sketch, "E383", {"start": v(-25.66, -18.07) * mm, "end": v(-27.47, -18.53) * mm});
            skLineSegment(sketch, "E384", {"start": v(-27.47, -18.53) * mm, "end": v(-29.35, -18.82) * mm});
            skLineSegment(sketch, "E385", {"start": v(-29.35, -18.82) * mm, "end": v(-31.28, -18.92) * mm});
            skLineSegment(sketch, "E386", {"start": v(-31.28, -18.92) * mm, "end": v(-33.21, -18.82) * mm});
            skLineSegment(sketch, "E387", {"start": v(-33.21, -18.82) * mm, "end": v(-35.09, -18.53) * mm});
            skLineSegment(sketch, "E388", {"start": v(-35.09, -18.53) * mm, "end": v(-36.9, -18.07) * mm});
            skLineSegment(sketch, "E389", {"start": v(-36.9, -18.07) * mm, "end": v(-38.64, -17.43) * mm});
            skLineSegment(sketch, "E390", {"start": v(-38.64, -17.43) * mm, "end": v(-40.29, -16.63) * mm});
            skLineSegment(sketch, "E391", {"start": v(-40.29, -16.63) * mm, "end": v(-41.85, -15.68) * mm});
            skLineSegment(sketch, "E392", {"start": v(-41.85, -15.68) * mm, "end": v(-43.3, -14.6) * mm});
            skLineSegment(sketch, "E393", {"start": v(-43.3, -14.6) * mm, "end": v(-44.65, -13.37) * mm});
            skLineSegment(sketch, "E394", {"start": v(-44.65, -13.37) * mm, "end": v(-45.87, -12.03) * mm});
            skLineSegment(sketch, "E395", {"start": v(-45.87, -12.03) * mm, "end": v(-46.96, -10.57) * mm});
            skLineSegment(sketch, "E396", {"start": v(-46.96, -10.57) * mm, "end": v(-47.91, -9) * mm});
            skLineSegment(sketch, "E397", {"start": v(-47.91, -9) * mm, "end": v(-48.7, -7.36) * mm});
            skLineSegment(sketch, "E398", {"start": v(-48.7, -7.36) * mm, "end": v(-49.34, -5.62) * mm});
            skLineSegment(sketch, "E399", {"start": v(-49.34, -5.62) * mm, "end": v(-49.81, -3.8) * mm});
            skLineSegment(sketch, "E400", {"start": v(-49.81, -3.8) * mm, "end": v(-50.1, -1.93) * mm});
            skLineSegment(sketch, "E401", {"start": v(-50.1, -1.93) * mm, "end": v(-50.2, 0) * mm});
            skLineSegment(sketch, "E402", {"start": v(-50.2, 0) * mm, "end": v(-50.1, 1.93) * mm});
            skLineSegment(sketch, "E403", {"start": v(-50.1, 1.93) * mm, "end": v(-49.81, 3.8) * mm});
            skLineSegment(sketch, "E404", {"start": v(-49.81, 3.8) * mm, "end": v(-49.34, 5.62) * mm});
            skLineSegment(sketch, "E405", {"start": v(-49.34, 5.62) * mm, "end": v(-48.7, 7.36) * mm});
            skLineSegment(sketch, "E406", {"start": v(-48.7, 7.36) * mm, "end": v(-47.91, 9) * mm});
            skLineSegment(sketch, "E407", {"start": v(-47.91, 9) * mm, "end": v(-46.96, 10.57) * mm});
            skLineSegment(sketch, "E408", {"start": v(-46.96, 10.57) * mm, "end": v(-45.87, 12.03) * mm});
            skLineSegment(sketch, "E409", {"start": v(-45.87, 12.03) * mm, "end": v(-44.65, 13.37) * mm});
            skLineSegment(sketch, "E410", {"start": v(-44.65, 13.37) * mm, "end": v(-43.3, 14.6) * mm});
            skLineSegment(sketch, "E411", {"start": v(-43.3, 14.6) * mm, "end": v(-41.85, 15.68) * mm});
            skLineSegment(sketch, "E412", {"start": v(-41.85, 15.68) * mm, "end": v(-40.29, 16.63) * mm});
            skLineSegment(sketch, "E413", {"start": v(-40.29, 16.63) * mm, "end": v(-38.64, 17.43) * mm});
            skLineSegment(sketch, "E414", {"start": v(-38.64, 17.43) * mm, "end": v(-36.9, 18.07) * mm});
            skLineSegment(sketch, "E415", {"start": v(-36.9, 18.07) * mm, "end": v(-35.09, 18.53) * mm});
            skLineSegment(sketch, "E416", {"start": v(-35.09, 18.53) * mm, "end": v(-33.21, 18.82) * mm});
            skLineSegment(sketch, "E417", {"start": v(-33.21, 18.82) * mm, "end": v(-31.28, 18.92) * mm});
            skLineSegment(sketch, "E418", {"start": v(-31.28, 18.92) * mm, "end": v(-29.35, 18.82) * mm});
            skLineSegment(sketch, "E419", {"start": v(-29.35, 18.82) * mm, "end": v(-27.47, 18.53) * mm});
            skLineSegment(sketch, "E420", {"start": v(-27.47, 18.53) * mm, "end": v(-25.66, 18.07) * mm});
            skLineSegment(sketch, "E421", {"start": v(-25.66, 18.07) * mm, "end": v(-23.92, 17.43) * mm});
            skLineSegment(sketch, "E422", {"start": v(-23.92, 17.43) * mm, "end": v(-22.27, 16.63) * mm});
            skLineSegment(sketch, "E423", {"start": v(-22.27, 16.63) * mm, "end": v(-20.7, 15.68) * mm});
            skLineSegment(sketch, "E424", {"start": v(-20.7, 15.68) * mm, "end": v(-19.25, 14.6) * mm});
            skLineSegment(sketch, "E425", {"start": v(-19.25, 14.6) * mm, "end": v(-17.9, 13.37) * mm});
            skLineSegment(sketch, "E426", {"start": v(-17.9, 13.37) * mm, "end": v(-16.69, 12.03) * mm});
            skLineSegment(sketch, "E427", {"start": v(-16.69, 12.03) * mm, "end": v(-15.6, 10.57) * mm});
            skLineSegment(sketch, "E428", {"start": v(-15.6, 10.57) * mm, "end": v(-14.65, 9) * mm});
            skLineSegment(sketch, "E429", {"start": v(-14.65, 9) * mm, "end": v(-13.85, 7.36) * mm});
            skLineSegment(sketch, "E430", {"start": v(-13.85, 7.36) * mm, "end": v(-13.21, 5.62) * mm});
            skLineSegment(sketch, "E431", {"start": v(-13.21, 5.62) * mm, "end": v(-12.75, 3.8) * mm});
            skLineSegment(sketch, "E432", {"start": v(-12.75, 3.8) * mm, "end": v(-12.46, 1.93) * mm});
            skLineSegment(sketch, "E433", {"start": v(-12.46, 1.93) * mm, "end": v(-12.36, 0) * mm});
            skLineSegment(sketch, "E434", {"start": v(-12.36, 0) * mm, "end": v(-12.46, -1.93) * mm});
            skLineSegment(sketch, "E435", {"start": v(-7.25, 4.38) * mm, "end": v(-7.28, 4.22) * mm});
            skLineSegment(sketch, "E436", {"start": v(-7.28, 4.22) * mm, "end": v(-7.31, 4.07) * mm});
            skLineSegment(sketch, "E437", {"start": v(-7.31, 4.07) * mm, "end": v(-7.37, 3.92) * mm});
            skLineSegment(sketch, "E438", {"start": v(-7.37, 3.92) * mm, "end": v(-7.44, 3.78) * mm});
            skLineSegment(sketch, "E439", {"start": v(-7.44, 3.78) * mm, "end": v(-7.52, 3.65) * mm});
            skLineSegment(sketch, "E440", {"start": v(-7.52, 3.65) * mm, "end": v(-7.6, 3.52) * mm});
            skLineSegment(sketch, "E441", {"start": v(-7.6, 3.52) * mm, "end": v(-7.71, 3.41) * mm});
            skLineSegment(sketch, "E442", {"start": v(-7.71, 3.41) * mm, "end": v(-7.82, 3.3) * mm});
            skLineSegment(sketch, "E443", {"start": v(-7.82, 3.3) * mm, "end": v(-7.95, 3.21) * mm});
            skLineSegment(sketch, "E444", {"start": v(-7.95, 3.21) * mm, "end": v(-8.08, 3.13) * mm});
            skLineSegment(sketch, "E445", {"start": v(-8.08, 3.13) * mm, "end": v(-8.22, 3.07) * mm});
            skLineSegment(sketch, "E446", {"start": v(-8.22, 3.07) * mm, "end": v(-8.37, 3.01) * mm});
            skLineSegment(sketch, "E447", {"start": v(-8.37, 3.01) * mm, "end": v(-8.52, 2.97) * mm});
            skLineSegment(sketch, "E448", {"start": v(-8.52, 2.97) * mm, "end": v(-8.68, 2.95) * mm});
            skLineSegment(sketch, "E449", {"start": v(-8.68, 2.95) * mm, "end": v(-8.84, 2.94) * mm});
            skLineSegment(sketch, "E450", {"start": v(-8.84, 2.94) * mm, "end": v(-9, 2.95) * mm});
            skLineSegment(sketch, "E451", {"start": v(-9, 2.95) * mm, "end": v(-9.17, 2.97) * mm});
            skLineSegment(sketch, "E452", {"start": v(-9.17, 2.97) * mm, "end": v(-9.32, 3.01) * mm});
            skLineSegment(sketch, "E453", {"start": v(-9.32, 3.01) * mm, "end": v(-9.47, 3.07) * mm});
            skLineSegment(sketch, "E454", {"start": v(-9.47, 3.07) * mm, "end": v(-9.6, 3.13) * mm});
            skLineSegment(sketch, "E455", {"start": v(-9.6, 3.13) * mm, "end": v(-9.74, 3.21) * mm});
            skLineSegment(sketch, "E456", {"start": v(-9.74, 3.21) * mm, "end": v(-9.86, 3.3) * mm});
            skLineSegment(sketch, "E457", {"start": v(-9.86, 3.3) * mm, "end": v(-9.97, 3.41) * mm});
            skLineSegment(sketch, "E458", {"start": v(-9.97, 3.41) * mm, "end": v(-10.08, 3.52) * mm});
            skLineSegment(sketch, "E459", {"start": v(-10.08, 3.52) * mm, "end": v(-10.17, 3.65) * mm});
            skLineSegment(sketch, "E460", {"start": v(-10.17, 3.65) * mm, "end": v(-10.25, 3.78) * mm});
            skLineSegment(sketch, "E461", {"start": v(-10.25, 3.78) * mm, "end": v(-10.32, 3.92) * mm});
            skLineSegment(sketch, "E462", {"start": v(-10.32, 3.92) * mm, "end": v(-10.37, 4.07) * mm});
            skLineSegment(sketch, "E463", {"start": v(-10.37, 4.07) * mm, "end": v(-10.41, 4.22) * mm});
            skLineSegment(sketch, "E464", {"start": v(-10.41, 4.22) * mm, "end": v(-10.43, 4.38) * mm});
            skLineSegment(sketch, "E465", {"start": v(-10.43, 4.38) * mm, "end": v(-10.44, 4.54) * mm});
            skLineSegment(sketch, "E466", {"start": v(-10.44, 4.54) * mm, "end": v(-10.43, 4.7) * mm});
            skLineSegment(sketch, "E467", {"start": v(-10.43, 4.7) * mm, "end": v(-10.41, 4.86) * mm});
            skLineSegment(sketch, "E468", {"start": v(-10.41, 4.86) * mm, "end": v(-10.37, 5.02) * mm});
            skLineSegment(sketch, "E469", {"start": v(-10.37, 5.02) * mm, "end": v(-10.32, 5.16) * mm});
            skLineSegment(sketch, "E470", {"start": v(-10.32, 5.16) * mm, "end": v(-10.25, 5.3) * mm});
            skLineSegment(sketch, "E471", {"start": v(-10.25, 5.3) * mm, "end": v(-10.17, 5.44) * mm});
            skLineSegment(sketch, "E472", {"start": v(-10.17, 5.44) * mm, "end": v(-10.08, 5.56) * mm});
            skLineSegment(sketch, "E473", {"start": v(-10.08, 5.56) * mm, "end": v(-9.97, 5.67) * mm});
            skLineSegment(sketch, "E474", {"start": v(-9.97, 5.67) * mm, "end": v(-9.86, 5.78) * mm});
            skLineSegment(sketch, "E475", {"start": v(-9.86, 5.78) * mm, "end": v(-9.74, 5.87) * mm});
            skLineSegment(sketch, "E476", {"start": v(-9.74, 5.87) * mm, "end": v(-9.6, 5.95) * mm});
            skLineSegment(sketch, "E477", {"start": v(-9.6, 5.95) * mm, "end": v(-9.47, 6.02) * mm});
            skLineSegment(sketch, "E478", {"start": v(-9.47, 6.02) * mm, "end": v(-9.32, 6.07) * mm});
            skLineSegment(sketch, "E479", {"start": v(-9.32, 6.07) * mm, "end": v(-9.17, 6.1) * mm});
            skLineSegment(sketch, "E480", {"start": v(-9.17, 6.1) * mm, "end": v(-9, 6.13) * mm});
            skLineSegment(sketch, "E481", {"start": v(-9, 6.13) * mm, "end": v(-8.84, 6.14) * mm});
            skLineSegment(sketch, "E482", {"start": v(-8.84, 6.14) * mm, "end": v(-8.68, 6.13) * mm});
            skLineSegment(sketch, "E483", {"start": v(-8.68, 6.13) * mm, "end": v(-8.52, 6.1) * mm});
            skLineSegment(sketch, "E484", {"start": v(-8.52, 6.1) * mm, "end": v(-8.37, 6.07) * mm});
            skLineSegment(sketch, "E485", {"start": v(-8.37, 6.07) * mm, "end": v(-8.22, 6.02) * mm});
            skLineSegment(sketch, "E486", {"start": v(-8.22, 6.02) * mm, "end": v(-8.08, 5.95) * mm});
            skLineSegment(sketch, "E487", {"start": v(-8.08, 5.95) * mm, "end": v(-7.95, 5.87) * mm});
            skLineSegment(sketch, "E488", {"start": v(-7.95, 5.87) * mm, "end": v(-7.82, 5.78) * mm});
            skLineSegment(sketch, "E489", {"start": v(-7.82, 5.78) * mm, "end": v(-7.71, 5.67) * mm});
            skLineSegment(sketch, "E490", {"start": v(-7.71, 5.67) * mm, "end": v(-7.6, 5.56) * mm});
            skLineSegment(sketch, "E491", {"start": v(-7.6, 5.56) * mm, "end": v(-7.52, 5.44) * mm});
            skLineSegment(sketch, "E492", {"start": v(-7.52, 5.44) * mm, "end": v(-7.44, 5.3) * mm});
            skLineSegment(sketch, "E493", {"start": v(-7.44, 5.3) * mm, "end": v(-7.37, 5.16) * mm});
            skLineSegment(sketch, "E494", {"start": v(-7.37, 5.16) * mm, "end": v(-7.31, 5.02) * mm});
            skLineSegment(sketch, "E495", {"start": v(-7.31, 5.02) * mm, "end": v(-7.28, 4.86) * mm});
            skLineSegment(sketch, "E496", {"start": v(-7.28, 4.86) * mm, "end": v(-7.25, 4.7) * mm});
            skLineSegment(sketch, "E497", {"start": v(-7.25, 4.7) * mm, "end": v(-7.24, 4.54) * mm});
            skLineSegment(sketch, "E498", {"start": v(-7.24, 4.54) * mm, "end": v(-7.25, 4.38) * mm});
            skLineSegment(sketch, "E499", {"start": v(51.91, -1.93) * mm, "end": v(51.62, -3.8) * mm});
            skLineSegment(sketch, "E500", {"start": v(51.62, -3.8) * mm, "end": v(51.16, -5.62) * mm});
            skLineSegment(sketch, "E501", {"start": v(51.16, -5.62) * mm, "end": v(50.52, -7.36) * mm});
            skLineSegment(sketch, "E502", {"start": v(50.52, -7.36) * mm, "end": v(49.72, -9) * mm});
            skLineSegment(sketch, "E503", {"start": v(49.72, -9) * mm, "end": v(48.77, -10.57) * mm});
            skLineSegment(sketch, "E504", {"start": v(48.77, -10.57) * mm, "end": v(47.68, -12.03) * mm});
            skLineSegment(sketch, "E505", {"start": v(47.68, -12.03) * mm, "end": v(46.46, -13.37) * mm});
            skLineSegment(sketch, "E506", {"start": v(46.46, -13.37) * mm, "end": v(45.12, -14.6) * mm});
            skLineSegment(sketch, "E507", {"start": v(45.12, -14.6) * mm, "end": v(43.66, -15.68) * mm});
            skLineSegment(sketch, "E508", {"start": v(43.66, -15.68) * mm, "end": v(42.1, -16.63) * mm});
            skLineSegment(sketch, "E509", {"start": v(42.1, -16.63) * mm, "end": v(40.45, -17.43) * mm});
            skLineSegment(sketch, "E510", {"start": v(40.45, -17.43) * mm, "end": v(38.71, -18.07) * mm});
            skLineSegment(sketch, "E511", {"start": v(38.71, -18.07) * mm, "end": v(36.9, -18.53) * mm});
            skLineSegment(sketch, "E512", {"start": v(36.9, -18.53) * mm, "end": v(35.02, -18.82) * mm});
            skLineSegment(sketch, "E513", {"start": v(35.02, -18.82) * mm, "end": v(33.1, -18.92) * mm});
            skLineSegment(sketch, "E514", {"start": v(33.1, -18.92) * mm, "end": v(31.16, -18.82) * mm});
            skLineSegment(sketch, "E515", {"start": v(31.16, -18.82) * mm, "end": v(29.28, -18.53) * mm});
            skLineSegment(sketch, "E516", {"start": v(29.28, -18.53) * mm, "end": v(27.47, -18.07) * mm});
            skLineSegment(sketch, "E517", {"start": v(27.47, -18.07) * mm, "end": v(25.73, -17.43) * mm});
            skLineSegment(sketch, "E518", {"start": v(25.73, -17.43) * mm, "end": v(24.08, -16.63) * mm});
            skLineSegment(sketch, "E519", {"start": v(24.08, -16.63) * mm, "end": v(22.52, -15.68) * mm});
            skLineSegment(sketch, "E520", {"start": v(22.52, -15.68) * mm, "end": v(21.07, -14.6) * mm});
            skLineSegment(sketch, "E521", {"start": v(21.07, -14.6) * mm, "end": v(19.72, -13.37) * mm});
            skLineSegment(sketch, "E522", {"start": v(19.72, -13.37) * mm, "end": v(18.5, -12.03) * mm});
            skLineSegment(sketch, "E523", {"start": v(18.5, -12.03) * mm, "end": v(17.4, -10.57) * mm});
            skLineSegment(sketch, "E524", {"start": v(17.4, -10.57) * mm, "end": v(16.46, -9) * mm});
            skLineSegment(sketch, "E525", {"start": v(16.46, -9) * mm, "end": v(15.66, -7.36) * mm});
            skLineSegment(sketch, "E526", {"start": v(15.66, -7.36) * mm, "end": v(15.03, -5.62) * mm});
            skLineSegment(sketch, "E527", {"start": v(15.03, -5.62) * mm, "end": v(14.56, -3.8) * mm});
            skLineSegment(sketch, "E528", {"start": v(14.56, -3.8) * mm, "end": v(14.27, -1.93) * mm});
            skLineSegment(sketch, "E529", {"start": v(14.27, -1.93) * mm, "end": v(14.17, 0) * mm});
            skLineSegment(sketch, "E530", {"start": v(14.17, 0) * mm, "end": v(14.27, 1.93) * mm});
            skLineSegment(sketch, "E531", {"start": v(14.27, 1.93) * mm, "end": v(14.56, 3.8) * mm});
            skLineSegment(sketch, "E532", {"start": v(14.56, 3.8) * mm, "end": v(15.03, 5.62) * mm});
            skLineSegment(sketch, "E533", {"start": v(15.03, 5.62) * mm, "end": v(15.66, 7.36) * mm});
            skLineSegment(sketch, "E534", {"start": v(15.66, 7.36) * mm, "end": v(16.46, 9) * mm});
            skLineSegment(sketch, "E535", {"start": v(16.46, 9) * mm, "end": v(17.4, 10.57) * mm});
            skLineSegment(sketch, "E536", {"start": v(17.4, 10.57) * mm, "end": v(18.5, 12.03) * mm});
            skLineSegment(sketch, "E537", {"start": v(18.5, 12.03) * mm, "end": v(19.72, 13.37) * mm});
            skLineSegment(sketch, "E538", {"start": v(19.72, 13.37) * mm, "end": v(21.07, 14.6) * mm});
            skLineSegment(sketch, "E539", {"start": v(21.07, 14.6) * mm, "end": v(22.52, 15.68) * mm});
            skLineSegment(sketch, "E540", {"start": v(22.52, 15.68) * mm, "end": v(24.08, 16.63) * mm});
            skLineSegment(sketch, "E541", {"start": v(24.08, 16.63) * mm, "end": v(25.73, 17.43) * mm});
            skLineSegment(sketch, "E542", {"start": v(25.73, 17.43) * mm, "end": v(27.47, 18.07) * mm});
            skLineSegment(sketch, "E543", {"start": v(27.47, 18.07) * mm, "end": v(29.28, 18.53) * mm});
            skLineSegment(sketch, "E544", {"start": v(29.28, 18.53) * mm, "end": v(31.16, 18.82) * mm});
            skLineSegment(sketch, "E545", {"start": v(31.16, 18.82) * mm, "end": v(33.1, 18.92) * mm});
            skLineSegment(sketch, "E546", {"start": v(33.1, 18.92) * mm, "end": v(35.02, 18.82) * mm});
            skLineSegment(sketch, "E547", {"start": v(35.02, 18.82) * mm, "end": v(36.9, 18.53) * mm});
            skLineSegment(sketch, "E548", {"start": v(36.9, 18.53) * mm, "end": v(38.71, 18.07) * mm});
            skLineSegment(sketch, "E549", {"start": v(38.71, 18.07) * mm, "end": v(40.45, 17.43) * mm});
            skLineSegment(sketch, "E550", {"start": v(40.45, 17.43) * mm, "end": v(42.1, 16.63) * mm});
            skLineSegment(sketch, "E551", {"start": v(42.1, 16.63) * mm, "end": v(43.66, 15.68) * mm});
            skLineSegment(sketch, "E552", {"start": v(43.66, 15.68) * mm, "end": v(45.12, 14.6) * mm});
            skLineSegment(sketch, "E553", {"start": v(45.12, 14.6) * mm, "end": v(46.46, 13.37) * mm});
            skLineSegment(sketch, "E554", {"start": v(46.46, 13.37) * mm, "end": v(47.68, 12.03) * mm});
            skLineSegment(sketch, "E555", {"start": v(47.68, 12.03) * mm, "end": v(48.77, 10.57) * mm});
            skLineSegment(sketch, "E556", {"start": v(48.77, 10.57) * mm, "end": v(49.72, 9) * mm});
            skLineSegment(sketch, "E557", {"start": v(49.72, 9) * mm, "end": v(50.52, 7.36) * mm});
            skLineSegment(sketch, "E558", {"start": v(50.52, 7.36) * mm, "end": v(51.16, 5.62) * mm});
            skLineSegment(sketch, "E559", {"start": v(51.16, 5.62) * mm, "end": v(51.62, 3.8) * mm});
            skLineSegment(sketch, "E560", {"start": v(51.62, 3.8) * mm, "end": v(51.91, 1.93) * mm});
            skLineSegment(sketch, "E561", {"start": v(51.91, 1.93) * mm, "end": v(52, 0) * mm});
            skLineSegment(sketch, "E562", {"start": v(52, 0) * mm, "end": v(51.91, -1.93) * mm});
            skSolve(sketch);
        }
        {
            var Q0;
            Q0 = qSketchRegion(id + "F0", true);
            extrude(context, id + "F1", {"entities" : qUnion([Q0]), "depth" : 6 * mm});
        }
    });
